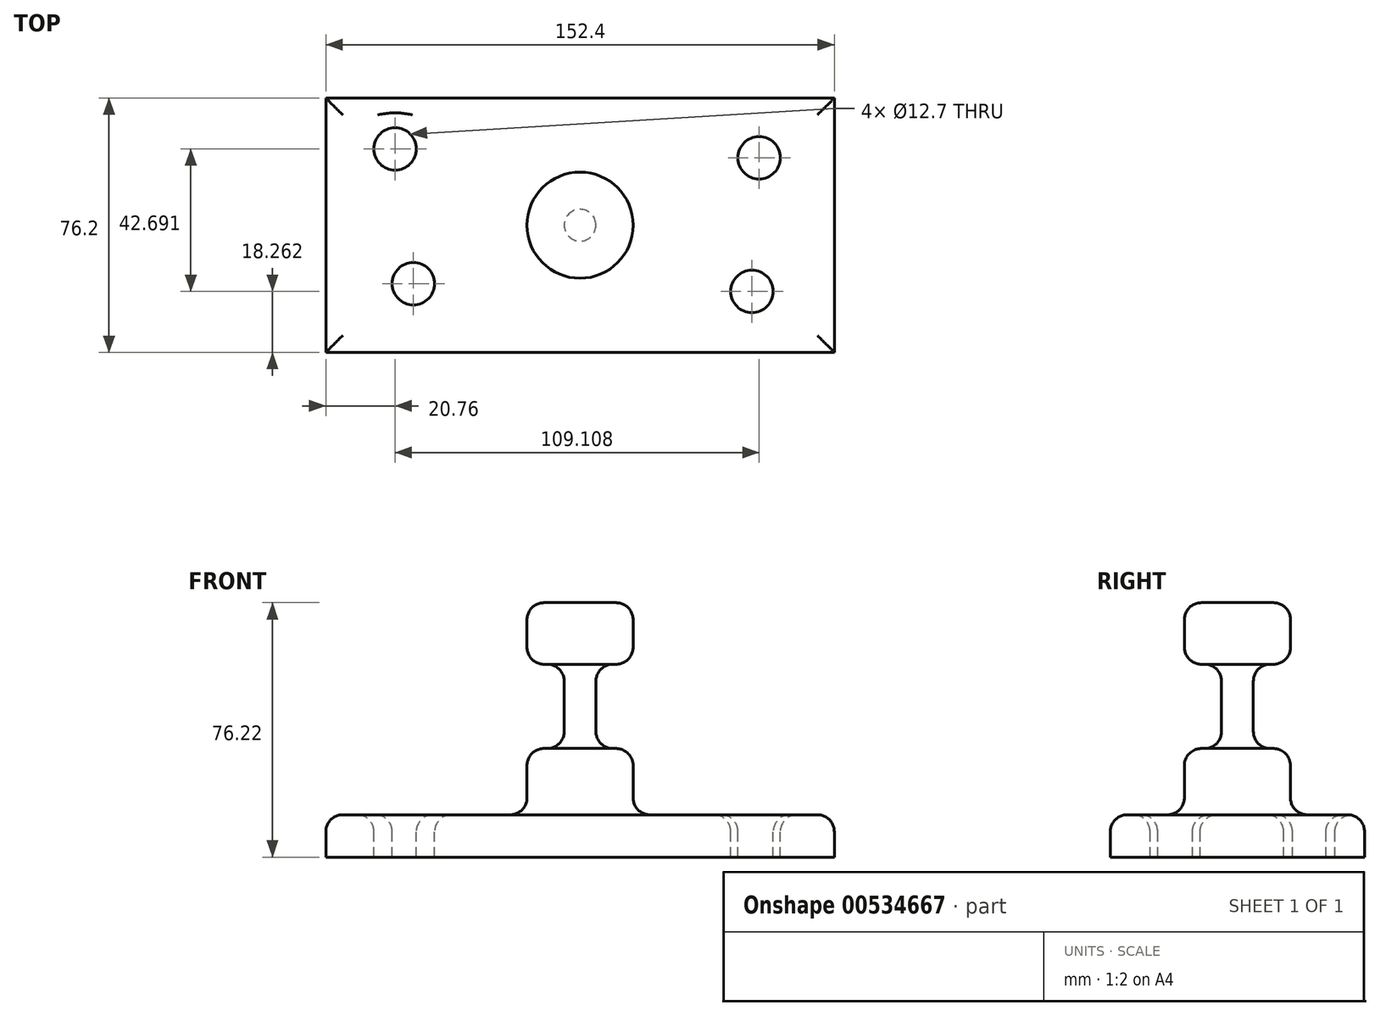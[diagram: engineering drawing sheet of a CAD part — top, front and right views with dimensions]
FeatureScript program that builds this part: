
annotation { "Feature Type Name" : "Feature", "Feature Type Description" : "" }
export const myFeature = defineFeature(function(context is Context, id is Id, definition is map)
    precondition{}
    {
        {
            var Q0;
            Q0=qCreatedBy(makeId("Top.planeOp"),FACE);
            var sketch = newSketch(context, id + "F0", { "sketchPlane" : qUnion([Q0])});
            skLineSegment(sketch, "E0.bottom", {"start": v(-76.2, 38.1) * mm, "end": v(76.2, 38.1) * mm});
            skLineSegment(sketch, "E0.top", {"start": v(-76.2, -38.1) * mm, "end": v(76.2, -38.1) * mm});
            skLineSegment(sketch, "E0.left", {"start": v(-76.2, 38.1) * mm, "end": v(-76.2, -38.1) * mm});
            skLineSegment(sketch, "E0.right", {"start": v(76.2, 38.1) * mm, "end": v(76.2, -38.1) * mm});
            skPoint(sketch, "E0.middle", {"position": v(0, 0) * mm});
            skSolve(sketch);
        }
        {
            var Q0;
            Q0 = qSketchRegion(id + "F0", true);
            extrude(context, id + "F1", {"entities" : qUnion([Q0]), "depth" : 12.7 * mm, "offsetDistance" : 25.4 * mm});
        }
        {
            var Q0;
            Q0=makeQuery(id+"F1.opExtrude","CAP_FACE",FACE,{"disambiguationData":[OSD([sQuery(id+"F0.wireOp",EDGE,"E0.bottom"),sQuery(id+"F0.wireOp",EDGE,"E0.top"),sQuery(id+"F0.wireOp",EDGE,"E0.left"),sQuery(id+"F0.wireOp",EDGE,"E0.right")])],"isStart":false});
            var sketch = newSketch(context, id + "F2", { "sketchPlane" : qUnion([Q0])});
            skCircle(sketch, "E1", {"center": v(-55.44, 22.85) * mm, "radius": 6.35 * mm});
            skCircle(sketch, "E2", {"center": v(-49.96, -17.53) * mm, "radius": 6.35 * mm});
            skCircle(sketch, "E3", {"center": v(53.67, 20.2) * mm, "radius": 6.35 * mm});
            skCircle(sketch, "E4", {"center": v(51.52, -19.84) * mm, "radius": 6.35 * mm});
            skSolve(sketch);
        }
        {
            var Q0;
            Q0=makeQuery(id+"F2.imprint","IMPRINT",FACE,{"disambiguationData":[TD([[makeQuery(id+"F2.imprint","IMPRINT",EDGE,{"derivedFrom":sQuery(id+"F2.wireOp",EDGE,"E1")}),1.0]])]});
            var Q1;
            Q1=makeQuery(id+"F2.imprint","IMPRINT",FACE,{"disambiguationData":[TD([[makeQuery(id+"F2.imprint","IMPRINT",EDGE,{"derivedFrom":sQuery(id+"F2.wireOp",EDGE,"E2")}),1.0]])]});
            var Q2;
            Q2=makeQuery(id+"F2.imprint","IMPRINT",FACE,{"disambiguationData":[TD([[makeQuery(id+"F2.imprint","IMPRINT",EDGE,{"derivedFrom":sQuery(id+"F2.wireOp",EDGE,"E4")}),1.0]])]});
            var Q3;
            Q3=makeQuery(id+"F2.imprint","IMPRINT",FACE,{"disambiguationData":[TD([[makeQuery(id+"F2.imprint","IMPRINT",EDGE,{"derivedFrom":sQuery(id+"F2.wireOp",EDGE,"E3")}),1.0]])]});
            extrude(context, id + "F3", {"entities" : qUnion([Q0, Q1, Q2, Q3]), "operationType" : NewBodyOperationType.REMOVE, "oppositeDirection" : true, "depth" : 25.4 * mm, "offsetDistance" : 25.4 * mm});
        }
        {
            var Q0;
            Q0=qCreatedBy(makeId("Front.planeOp"),FACE);
            var sketch = newSketch(context, id + "F4", { "sketchPlane" : qUnion([Q0])});
            skLineSegment(sketch, "E5.bottom", {"start": v(0, 12.7) * mm, "end": v(15.9, 12.7) * mm});
            skLineSegment(sketch, "E5.top", {"start": v(0, 76.22) * mm, "end": v(15.9, 76.22) * mm});
            skLineSegment(sketch, "E5.left", {"start": v(0, 12.7) * mm, "end": v(0, 76.22) * mm});
            skLineSegment(sketch, "E5.right", {"start": v(15.9, 12.7) * mm, "end": v(15.9, 76.22) * mm});
            skSolve(sketch);
        }
        {
            var Q0;
            Q0 = qSketchRegion(id + "F4", true);
            var Q1;
            Q1=sQuery(id+"F4.wireOp",EDGE,"E5.left");
            revolve(context, id + "F5", {"operationType" : NewBodyOperationType.ADD, "entities" : qUnion([Q0]), "axis" : qUnion([Q1]), "revolveType" : RevolveType.FULL});
        }
        {
            var Q0;
            Q0=qCreatedBy(makeId("Front.planeOp"),FACE);
            var sketch = newSketch(context, id + "F6", { "sketchPlane" : qUnion([Q0])});
            skLineSegment(sketch, "E6.bottom", {"start": v(15.9, 57.79) * mm, "end": v(4.77, 57.79) * mm});
            skLineSegment(sketch, "E6.top", {"start": v(15.9, 32.54) * mm, "end": v(4.77, 32.54) * mm});
            skLineSegment(sketch, "E6.left", {"start": v(15.9, 57.79) * mm, "end": v(15.9, 32.54) * mm});
            skLineSegment(sketch, "E6.right", {"start": v(4.77, 57.79) * mm, "end": v(4.77, 32.54) * mm});
            skSolve(sketch);
        }
        {
            var Q0;
            Q0 = qSketchRegion(id + "F6", true);
            var Q1;
            Q1=sQuery(id+"F4.wireOp",EDGE,"E5.left");
            revolve(context, id + "F7", {"operationType" : NewBodyOperationType.REMOVE, "entities" : qUnion([Q0]), "axis" : qUnion([Q1]), "revolveType" : RevolveType.FULL, "oppositeDirection" : true});
        }
        {
            var Q0;
            Q0=makeQuery(id+"F5.opRevolve","SWEPT_FACE",FACE,{"disambiguationData":[OSD([sQuery(id+"F4.wireOp",EDGE,"E5.top")])]});
            fillet(context, id + "F8", {"entities" : qUnion([Q0]), "radius" : 5.08 * mm, "tangentPropagation" : true, "allowEdgeOverflow" : false});
        }
        {
            var Q0;
            Q0=makeQuery(id+"F7.boolean.opBoolean","COPY",FACE,{"derivedFrom":makeQuery(id+"F7.opRevolve","SWEPT_FACE",FACE,{"disambiguationData":[OSD([sQuery(id+"F6.wireOp",EDGE,"E6.bottom")])]})});
            fillet(context, id + "F9", {"entities" : qUnion([Q0]), "radius" : 5.08 * mm, "tangentPropagation" : true, "allowEdgeOverflow" : false});
        }
        {
            var Q0;
            Q0=makeQuery(id+"F1.opExtrude","CAP_FACE",FACE,{"disambiguationData":[OSD([sQuery(id+"F0.wireOp",EDGE,"E0.bottom"),sQuery(id+"F0.wireOp",EDGE,"E0.top"),sQuery(id+"F0.wireOp",EDGE,"E0.left"),sQuery(id+"F0.wireOp",EDGE,"E0.right")])],"isStart":false});
            fillet(context, id + "F10", {"entities" : qUnion([Q0]), "radius" : 5.08 * mm, "tangentPropagation" : true, "allowEdgeOverflow" : false});
        }
        {
            var Q0;
            Q0=makeQuery(id+"F7.boolean.opBoolean","COPY",FACE,{"derivedFrom":makeQuery(id+"F7.opRevolve","SWEPT_FACE",FACE,{"disambiguationData":[OSD([sQuery(id+"F6.wireOp",EDGE,"E6.top")])]})});
            fillet(context, id + "F11", {"entities" : qUnion([Q0]), "radius" : 5.08 * mm, "tangentPropagation" : true, "allowEdgeOverflow" : false});
        }
    });
